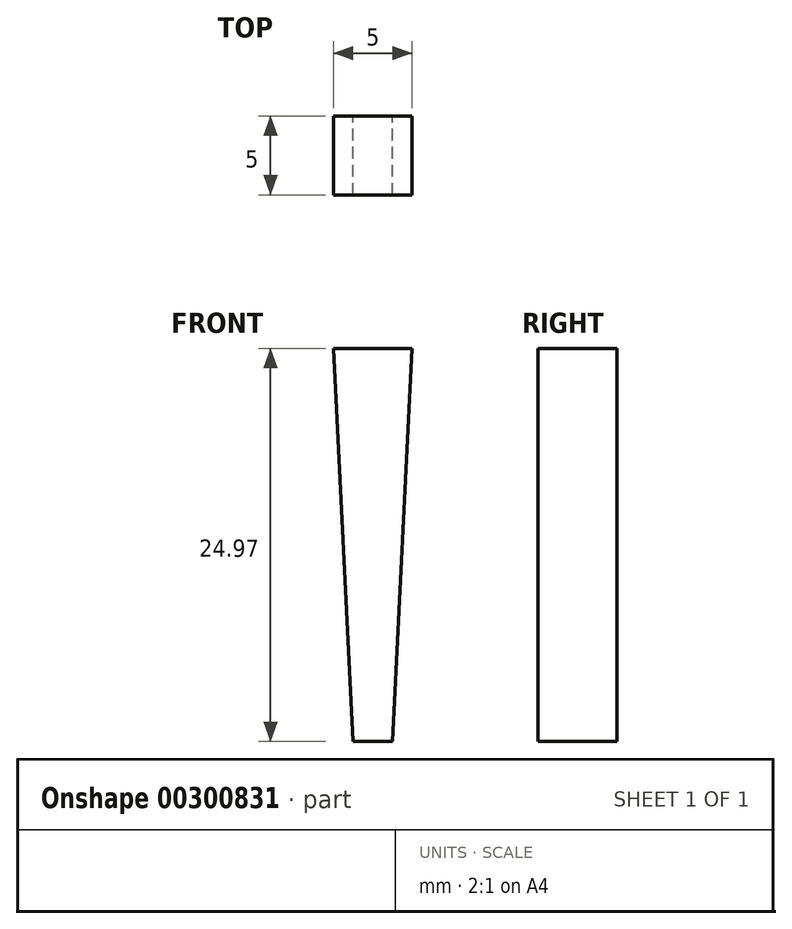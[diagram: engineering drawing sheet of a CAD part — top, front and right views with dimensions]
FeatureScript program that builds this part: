
annotation { "Feature Type Name" : "Feature", "Feature Type Description" : "" }
export const myFeature = defineFeature(function(context is Context, id is Id, definition is map)
    precondition{}
    {
        {
            var Q0;
            Q0=qCreatedBy(makeId("Front.planeOp"),FACE);
            var sketch = newSketch(context, id + "F0", { "sketchPlane" : qUnion([Q0])});
            skLineSegment(sketch, "E0", {"start": v(0, 0) * mm, "end": v(50, 0) * mm});
            skLineSegment(sketch, "E1", {"start": v(50, 0) * mm, "end": v(25, -499.37) * mm});
            skLineSegment(sketch, "E2", {"start": v(25, -499.37) * mm, "end": v(0, -499.37) * mm});
            skLineSegment(sketch, "E3", {"start": v(0, 0) * mm, "end": v(0, -499.37) * mm});
            skPoint(sketch, "E4", {"position": v(0, -249.69) * mm});
            skLineSegment(sketch, "E5", {"start": v(0, 0) * mm, "end": v(-50, 0) * mm});
            skLineSegment(sketch, "E6", {"start": v(-50, 0) * mm, "end": v(-25, -499.37) * mm});
            skLineSegment(sketch, "E7", {"start": v(-25, -499.37) * mm, "end": v(0, -499.37) * mm});
            skSolve(sketch);
        }
        {
            var Q0;
            Q0=makeQuery(id+"F0.imprint","IMPRINT",FACE,{"disambiguationData":[TD([[makeQuery(id+"F0.imprint","IMPRINT",EDGE,{"derivedFrom":sQuery(id+"F0.wireOp",EDGE,"E3")}),-1.0]])]});
            var Q1;
            Q1=makeQuery(id+"F0.imprint","IMPRINT",FACE,{"disambiguationData":[TD([[makeQuery(id+"F0.imprint","IMPRINT",EDGE,{"derivedFrom":sQuery(id+"F0.wireOp",EDGE,"E0")}),-1.0]])]});
            extrude(context, id + "F1", {"entities" : qUnion([Q0, Q1]), "depth" : 100 * mm});
        }
        {
            var Q0;
            Q0=makeQuery(id+"F1.opExtrude","SWEPT_BODY",BODY,{"disambiguationData":[OSD([sQuery(id+"F0.wireOp",EDGE,"E0"),sQuery(id+"F0.wireOp",EDGE,"E1"),sQuery(id+"F0.wireOp",EDGE,"E2"),sQuery(id+"F0.wireOp",EDGE,"E5"),sQuery(id+"F0.wireOp",EDGE,"E6"),sQuery(id+"F0.wireOp",EDGE,"E7")])]});
            var Q1;
            Q1=qCreatedBy(makeId("Origin.pointOp"),VERTEX);
            transform(context, id + "F2", {"entities" : qUnion([Q0]), "transformType" : TransformType.SCALE_UNIFORMLY, "scale" : 0.05, "scalePoint" : qUnion([Q1]), "makeCopy" : false});
        }
    });
